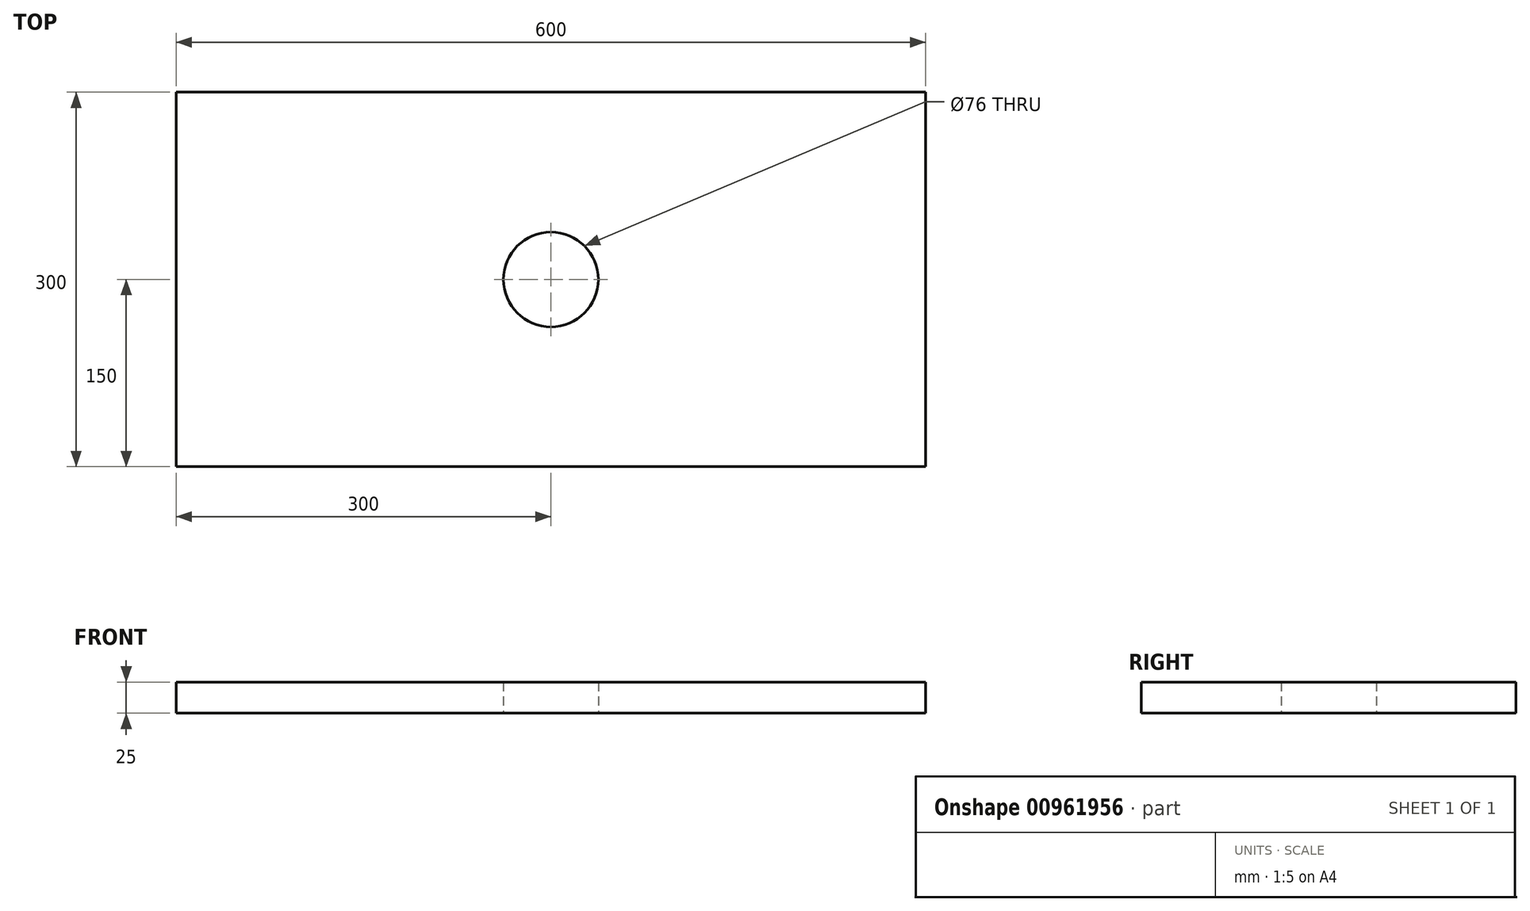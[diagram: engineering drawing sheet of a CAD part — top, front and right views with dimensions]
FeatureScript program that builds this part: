
annotation { "Feature Type Name" : "Feature", "Feature Type Description" : "" }
export const myFeature = defineFeature(function(context is Context, id is Id, definition is map)
    precondition{}
    {
        {
            var Q0;
            Q0=qCreatedBy(makeId("Top.planeOp"),FACE);
            var sketch = newSketch(context, id + "F0", { "sketchPlane" : qUnion([Q0])});
            skLineSegment(sketch, "E0.bottom", {"start": v(300, -150) * mm, "end": v(-300, -150) * mm});
            skLineSegment(sketch, "E0.top", {"start": v(300, 150) * mm, "end": v(-300, 150) * mm});
            skLineSegment(sketch, "E0.left", {"start": v(300, -150) * mm, "end": v(300, 150) * mm});
            skLineSegment(sketch, "E0.right", {"start": v(-300, -150) * mm, "end": v(-300, 150) * mm});
            skPoint(sketch, "E0.middle", {"position": v(0, 0) * mm});
            skCircle(sketch, "E1", {"center": v(0, 0) * mm, "radius": 38 * mm});
            skSolve(sketch);
        }
        {
            var Q0;
            Q0=makeQuery(id+"F0.imprint","IMPRINT",FACE,{"disambiguationData":[TD([[makeQuery(id+"F0.imprint","IMPRINT",EDGE,{"derivedFrom":sQuery(id+"F0.wireOp",EDGE,"E0.bottom")}),-1.0]])]});
            extrude(context, id + "F1", {"entities" : qUnion([Q0]), "depth" : 25 * mm, "offsetDistance" : 25.4 * mm});
        }
    });
